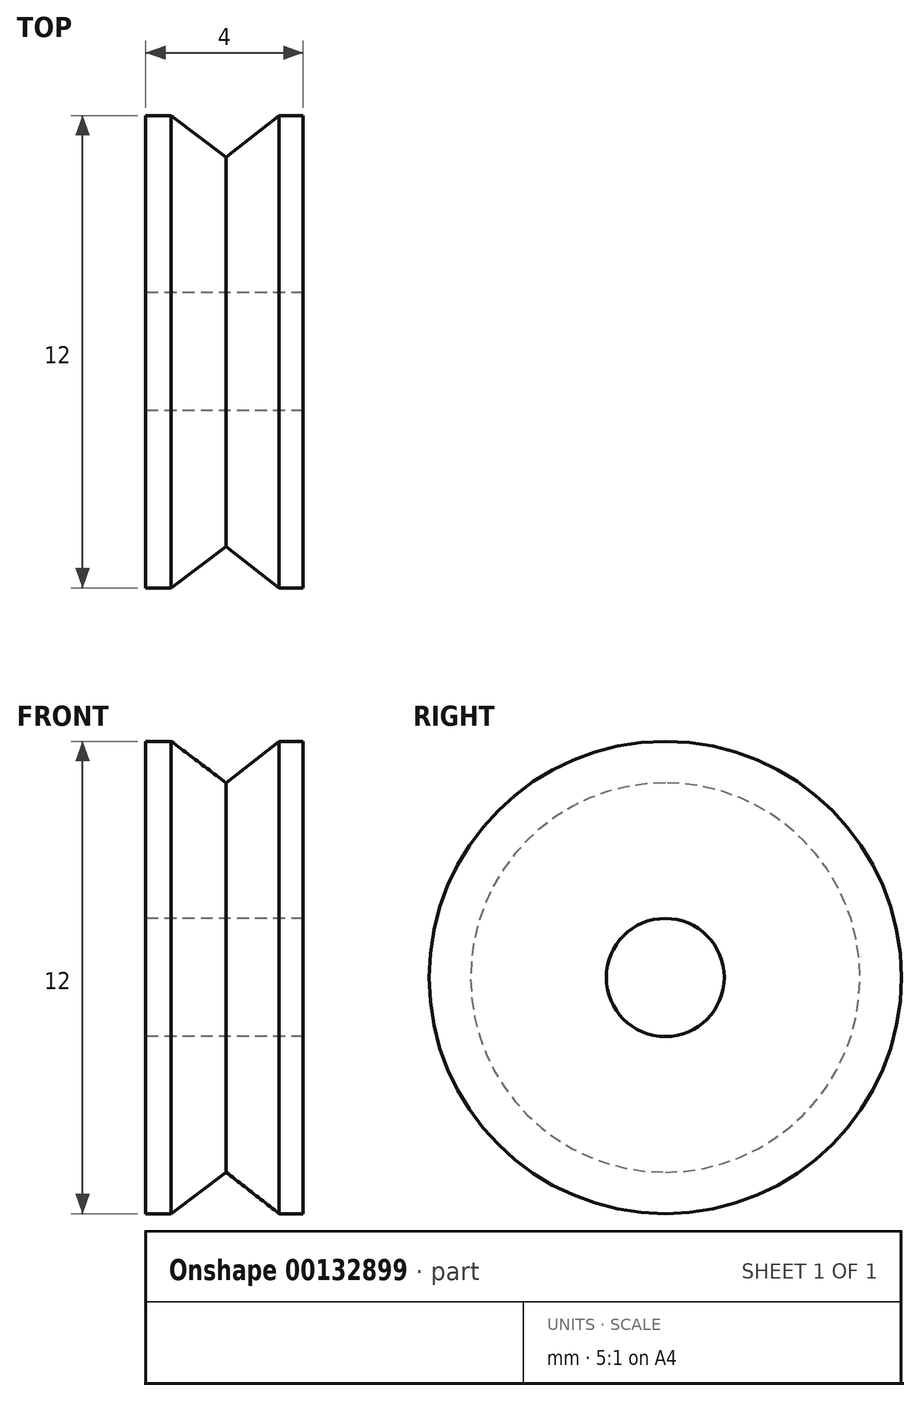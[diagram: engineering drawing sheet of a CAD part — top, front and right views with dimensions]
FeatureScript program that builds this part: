
annotation { "Feature Type Name" : "Feature", "Feature Type Description" : "" }
export const myFeature = defineFeature(function(context is Context, id is Id, definition is map)
    precondition{}
    {
        {
            var Q0;
            Q0=qCreatedBy(makeId("Right.planeOp"),FACE);
            var sketch = newSketch(context, id + "F0", { "sketchPlane" : qUnion([Q0])});
            skCircle(sketch, "E0", {"center": v(0, 0) * mm, "radius": 6 * mm});
            skCircle(sketch, "E1", {"center": v(0, 0) * mm, "radius": 1.5 * mm});
            skSolve(sketch);
        }
        {
            var Q0;
            Q0 = qSketchRegion(id + "F0", true);
            extrude(context, id + "F1", {"entities" : qUnion([Q0]), "depth" : 4 * mm});
        }
        {
            var Q0;
            Q0=qCreatedBy(makeId("Front.planeOp"),FACE);
            var sketch = newSketch(context, id + "F2", { "sketchPlane" : qUnion([Q0])});
            skLineSegment(sketch, "E2", {"start": v(0, 6.5) * mm, "end": v(4.02, 6.5) * mm});
            skLineSegment(sketch, "E3", {"start": v(4.02, 6.5) * mm, "end": v(2.04, 4.95) * mm});
            skLineSegment(sketch, "E4", {"start": v(2.04, 4.95) * mm, "end": v(0, 6.5) * mm});
            skSolve(sketch);
        }
        {
            var Q0;
            Q0=makeQuery(id+"F2.imprint","IMPRINT",FACE,{"disambiguationData":[TD([[makeQuery(id+"F2.imprint","IMPRINT",EDGE,{"derivedFrom":sQuery(id+"F2.wireOp",EDGE,"E2")}),-1.0]])]});
            var Q1;
            Q1=makeQuery(id+"F1.opExtrude","CAP_EDGE",EDGE,{"disambiguationData":[OSD([sQuery(id+"F0.wireOp",EDGE,"E1")])],"isStart":true});
            revolve(context, id + "F3", {"operationType" : NewBodyOperationType.REMOVE, "entities" : qUnion([Q0]), "axis" : qUnion([Q1]), "revolveType" : RevolveType.FULL, "oppositeDirection" : true});
        }
    });
